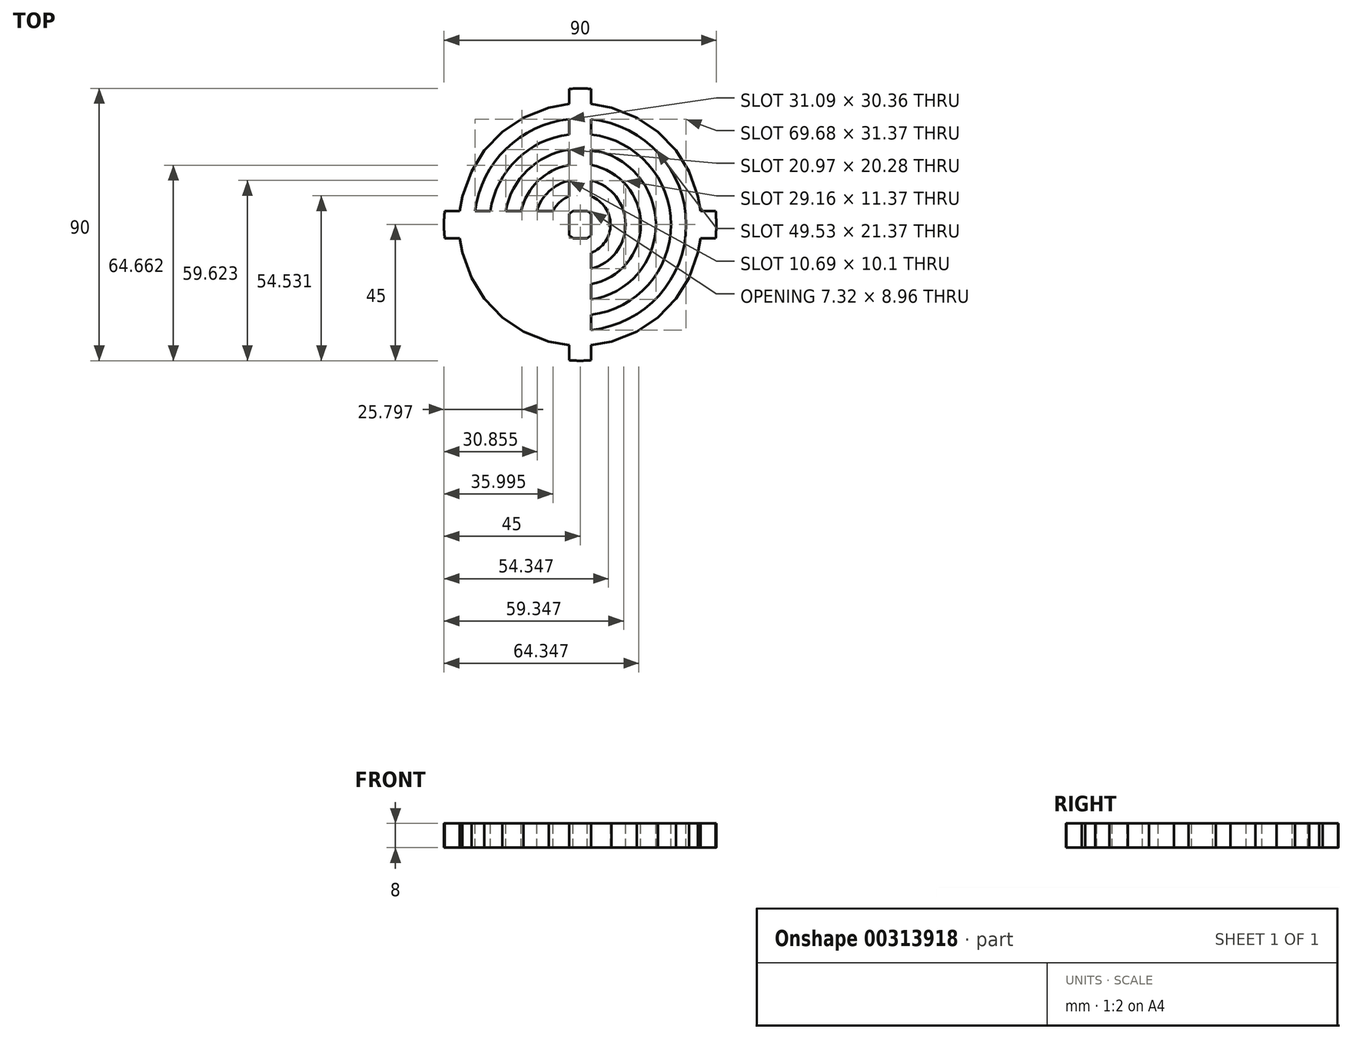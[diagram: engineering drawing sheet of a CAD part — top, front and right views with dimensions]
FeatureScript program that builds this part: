
annotation { "Feature Type Name" : "Feature", "Feature Type Description" : "" }
export const myFeature = defineFeature(function(context is Context, id is Id, definition is map)
    precondition{}
    {
        {
            var Q0;
            Q0=qCreatedBy(makeId("Top.planeOp"),FACE);
            var sketch = newSketch(context, id + "F0", { "sketchPlane" : qUnion([Q0])});
            skCircle(sketch, "E0", {"center": v(0, 0) * mm, "radius": 45 * mm});
            skSolve(sketch);
        }
        {
            var Q0;
            Q0=makeQuery(id+"F0.imprint","IMPRINT",FACE,{"disambiguationData":[TD([[makeQuery(id+"F0.imprint","IMPRINT",EDGE,{"derivedFrom":sQuery(id+"F0.wireOp",EDGE,"E0")}),1.0]])]});
            extrude(context, id + "F1", {"entities" : qUnion([Q0]), "depth" : 8 * mm});
        }
        {
            var Q0;
            Q0=makeQuery(id+"F1.opExtrude","CAP_FACE",FACE,{"disambiguationData":[OSD([sQuery(id+"F0.wireOp",EDGE,"E0")])],"isStart":false});
            var sketch = newSketch(context, id + "F2", { "sketchPlane" : qUnion([Q0])});
            skLineSegment(sketch, "E1", {"start": v(0, 50.25) * mm, "end": v(0, -49.39) * mm, "construction": true});
            skLineSegment(sketch, "E2", {"start": v(-52.78, 0) * mm, "end": v(52.32, 0) * mm, "construction": true});
            skCircle(sketch, "E3", {"center": v(0, 0) * mm, "radius": 40.03 * mm, "construction": true});
            skLineSegment(sketch, "E4", {"start": v(-3.66, 44.85) * mm, "end": v(-3.66, 39.87) * mm});
            skLineSegment(sketch, "E5", {"start": v(-3.66, 39.87) * mm, "end": v(-10.32, 38.68) * mm});
            skLineSegment(sketch, "E6", {"start": v(-10.32, 38.68) * mm, "end": v(-18.69, 35.4) * mm});
            skLineSegment(sketch, "E7", {"start": v(-18.69, 35.4) * mm, "end": v(-25.77, 30.64) * mm});
            skLineSegment(sketch, "E8", {"start": v(-25.77, 30.64) * mm, "end": v(-31.64, 24.53) * mm});
            skLineSegment(sketch, "E9", {"start": v(-31.64, 24.53) * mm, "end": v(-35.95, 17.62) * mm});
            skLineSegment(sketch, "E10", {"start": v(-35.95, 17.62) * mm, "end": v(-38.94, 9.29) * mm});
            skLineSegment(sketch, "E11", {"start": v(-38.94, 9.29) * mm, "end": v(-39.78, 4.48) * mm});
            skLineSegment(sketch, "E12", {"start": v(-39.78, 4.48) * mm, "end": v(-50.5, 4.48) * mm});
            skLineSegment(sketch, "E13", {"start": v(-50.5, 4.48) * mm, "end": v(-45.74, 26.13) * mm});
            skLineSegment(sketch, "E14", {"start": v(-45.74, 26.13) * mm, "end": v(-30.42, 39.87) * mm});
            skLineSegment(sketch, "E15", {"start": v(-30.42, 39.87) * mm, "end": v(-14.4, 46.73) * mm});
            skLineSegment(sketch, "E16", {"start": v(-14.4, 46.73) * mm, "end": v(-3.66, 46.73) * mm});
            skLineSegment(sketch, "E17", {"start": v(-3.66, 46.73) * mm, "end": v(-3.66, 44.85) * mm});
            skLineSegment(sketch, "E18.MirrorCS", {"start": v(3.66, 46.73) * mm, "end": v(3.66, 44.85) * mm});
            skLineSegment(sketch, "E19.MirrorCS", {"start": v(18.69, 35.4) * mm, "end": v(25.77, 30.64) * mm});
            skLineSegment(sketch, "E20.MirrorCS", {"start": v(10.32, 38.68) * mm, "end": v(18.69, 35.4) * mm});
            skLineSegment(sketch, "E21.MirrorCS", {"start": v(25.77, 30.64) * mm, "end": v(31.64, 24.53) * mm});
            skLineSegment(sketch, "E22.MirrorCS", {"start": v(3.66, 39.87) * mm, "end": v(10.32, 38.68) * mm});
            skLineSegment(sketch, "E23.MirrorCS", {"start": v(31.64, 24.53) * mm, "end": v(35.95, 17.62) * mm});
            skLineSegment(sketch, "E24.MirrorCS", {"start": v(3.66, 44.85) * mm, "end": v(3.66, 39.87) * mm});
            skLineSegment(sketch, "E25.MirrorCS", {"start": v(35.95, 17.62) * mm, "end": v(38.94, 9.29) * mm});
            skLineSegment(sketch, "E26.MirrorCS", {"start": v(38.94, 9.29) * mm, "end": v(39.78, 4.48) * mm});
            skLineSegment(sketch, "E27.MirrorCS", {"start": v(52.78, 0) * mm, "end": v(-52.32, 0) * mm, "construction": true});
            skLineSegment(sketch, "E28.MirrorCS", {"start": v(39.78, 4.48) * mm, "end": v(50.5, 4.48) * mm});
            skLineSegment(sketch, "E29.MirrorCS", {"start": v(14.4, 46.73) * mm, "end": v(3.66, 46.73) * mm});
            skLineSegment(sketch, "E30.MirrorCS", {"start": v(45.74, 26.13) * mm, "end": v(30.42, 39.87) * mm});
            skLineSegment(sketch, "E31.MirrorCS", {"start": v(50.5, 4.48) * mm, "end": v(45.74, 26.13) * mm});
            skLineSegment(sketch, "E32.MirrorCS", {"start": v(30.42, 39.87) * mm, "end": v(14.4, 46.73) * mm});
            skLineSegment(sketch, "E33.MirrorCS", {"start": v(3.66, -46.73) * mm, "end": v(3.66, -44.85) * mm});
            skLineSegment(sketch, "E34.MirrorCS", {"start": v(-3.66, -46.73) * mm, "end": v(-3.66, -44.85) * mm});
            skLineSegment(sketch, "E35.MirrorCS", {"start": v(10.32, -38.68) * mm, "end": v(18.69, -35.4) * mm});
            skLineSegment(sketch, "E36.MirrorCS", {"start": v(38.94, -9.29) * mm, "end": v(39.78, -4.48) * mm});
            skLineSegment(sketch, "E37.MirrorCS", {"start": v(18.69, -35.4) * mm, "end": v(25.77, -30.64) * mm});
            skLineSegment(sketch, "E38.MirrorCS", {"start": v(31.64, -24.53) * mm, "end": v(35.95, -17.62) * mm});
            skLineSegment(sketch, "E39.MirrorCS", {"start": v(50.5, -4.48) * mm, "end": v(45.74, -26.13) * mm});
            skLineSegment(sketch, "E40.MirrorCS", {"start": v(-50.5, -4.48) * mm, "end": v(-45.74, -26.13) * mm});
            skLineSegment(sketch, "E41.MirrorCS", {"start": v(35.95, -17.62) * mm, "end": v(38.94, -9.29) * mm});
            skLineSegment(sketch, "E42.MirrorCS", {"start": v(-39.78, -4.48) * mm, "end": v(-50.5, -4.48) * mm});
            skLineSegment(sketch, "E43.MirrorCS", {"start": v(-38.94, -9.29) * mm, "end": v(-39.78, -4.48) * mm});
            skLineSegment(sketch, "E44.MirrorCS", {"start": v(-35.95, -17.62) * mm, "end": v(-38.94, -9.29) * mm});
            skLineSegment(sketch, "E45.MirrorCS", {"start": v(-31.64, -24.53) * mm, "end": v(-35.95, -17.62) * mm});
            skLineSegment(sketch, "E46.MirrorCS", {"start": v(-25.77, -30.64) * mm, "end": v(-31.64, -24.53) * mm});
            skLineSegment(sketch, "E47.MirrorCS", {"start": v(-18.69, -35.4) * mm, "end": v(-25.77, -30.64) * mm});
            skLineSegment(sketch, "E48.MirrorCS", {"start": v(-10.32, -38.68) * mm, "end": v(-18.69, -35.4) * mm});
            skLineSegment(sketch, "E49.MirrorCS", {"start": v(-3.66, -39.87) * mm, "end": v(-10.32, -38.68) * mm});
            skLineSegment(sketch, "E50.MirrorCS", {"start": v(-3.66, -44.85) * mm, "end": v(-3.66, -39.87) * mm});
            skLineSegment(sketch, "E51.MirrorCS", {"start": v(39.78, -4.48) * mm, "end": v(50.5, -4.48) * mm});
            skLineSegment(sketch, "E52.MirrorCS", {"start": v(45.74, -26.13) * mm, "end": v(30.42, -39.87) * mm});
            skLineSegment(sketch, "E53.MirrorCS", {"start": v(3.66, -39.87) * mm, "end": v(10.32, -38.68) * mm});
            skLineSegment(sketch, "E54.MirrorCS", {"start": v(30.42, -39.87) * mm, "end": v(14.4, -46.73) * mm});
            skLineSegment(sketch, "E55.MirrorCS", {"start": v(-45.74, -26.13) * mm, "end": v(-30.42, -39.87) * mm});
            skLineSegment(sketch, "E56.MirrorCS", {"start": v(25.77, -30.64) * mm, "end": v(31.64, -24.53) * mm});
            skLineSegment(sketch, "E57.MirrorCS", {"start": v(-30.42, -39.87) * mm, "end": v(-14.4, -46.73) * mm});
            skLineSegment(sketch, "E58.MirrorCS", {"start": v(14.4, -46.73) * mm, "end": v(3.66, -46.73) * mm});
            skLineSegment(sketch, "E59.MirrorCS", {"start": v(3.66, -44.85) * mm, "end": v(3.66, -39.87) * mm});
            skLineSegment(sketch, "E60.MirrorCS", {"start": v(-14.4, -46.73) * mm, "end": v(-3.66, -46.73) * mm});
            skSolve(sketch);
        }
        {
            var Q0;
            {var subQ0=sQuery(id+"F2.wireOp",EDGE,"E13");Q0=makeQuery(id+"F2.imprint","IMPRINT",FACE,{"disambiguationData":[TD([[makeQuery(id+"F2.imprint","IMPRINT",EDGE,{"derivedFrom":subQ0}),-1.0]])]});}
            var Q1;
            {var subQ0=sQuery(id+"F2.wireOp",EDGE,"E4");Q1=makeQuery(id+"F2.imprint","IMPRINT",FACE,{"disambiguationData":[TD([[makeQuery(id+"F2.imprint","IMPRINT",EDGE,{"derivedFrom":subQ0}),-1.0]])]});}
            var Q2;
            Q2=makeQuery(id+"F2.imprint","IMPRINT",FACE,{"disambiguationData":[TD([[makeQuery(id+"F2.imprint","IMPRINT",EDGE,{"derivedFrom":sQuery(id+"F2.wireOp",EDGE,"E19.MirrorCS")}),1.0]])]});
            var Q3;
            {var subQ0=sQuery(id+"F2.wireOp",EDGE,"E18.MirrorCS");Q3=makeQuery(id+"F2.imprint","IMPRINT",FACE,{"disambiguationData":[TD([[makeQuery(id+"F2.imprint","IMPRINT",EDGE,{"derivedFrom":subQ0}),1.0]])]});}
            var Q4;
            Q4=makeQuery(id+"F2.imprint","IMPRINT",FACE,{"disambiguationData":[TD([[makeQuery(id+"F2.imprint","IMPRINT",EDGE,{"derivedFrom":sQuery(id+"F2.wireOp",EDGE,"E35.MirrorCS")}),-1.0]])]});
            var Q5;
            {var subQ4=sQuery(id+"F2.wireOp",EDGE,"E33.MirrorCS");Q5=makeQuery(id+"F2.imprint","IMPRINT",FACE,{"disambiguationData":[TD([[makeQuery(id+"F2.imprint","IMPRINT",EDGE,{"derivedFrom":subQ4}),-1.0]])]});}
            var Q6;
            {var subQ4=sQuery(id+"F2.wireOp",EDGE,"E43.MirrorCS");Q6=makeQuery(id+"F2.imprint","IMPRINT",FACE,{"disambiguationData":[TD([[makeQuery(id+"F2.imprint","IMPRINT",EDGE,{"derivedFrom":subQ4}),1.0]])]});}
            var Q7;
            {var subQ0=sQuery(id+"F2.wireOp",EDGE,"E34.MirrorCS");Q7=makeQuery(id+"F2.imprint","IMPRINT",FACE,{"disambiguationData":[TD([[makeQuery(id+"F2.imprint","IMPRINT",EDGE,{"derivedFrom":subQ0}),1.0]])]});}
            extrude(context, id + "F3", {"entities" : qUnion([Q0, Q1, Q2, Q3, Q4, Q5, Q6, Q7]), "operationType" : NewBodyOperationType.REMOVE, "oppositeDirection" : true, "depth" : 25 * mm});
        }
        {
            var Q0;
            Q0=makeQuery(id+"F1.opExtrude","CAP_FACE",FACE,{"disambiguationData":[OSD([sQuery(id+"F0.wireOp",EDGE,"E0")])],"isStart":false});
            var sketch = newSketch(context, id + "F4", { "sketchPlane" : qUnion([Q0])});
            skLineSegment(sketch, "E61", {"start": v(0, 48.4) * mm, "end": v(0, -49.9) * mm, "construction": true});
            skPoint(sketch, "E61.endSnap0", {"position": v(0, -45) * mm});
            skPoint(sketch, "E62.endSnap0", {"position": v(-45, 0) * mm});
            skPoint(sketch, "E63.endSnap0", {"position": v(45, 0) * mm});
            skLineSegment(sketch, "E64", {"start": v(-52.35, 0) * mm, "end": v(55.1, 0) * mm, "construction": true});
            skCircle(sketch, "E65", {"center": v(0, 0) * mm, "radius": 35.03 * mm});
            skCircle(sketch, "E66", {"center": v(0, 0) * mm, "radius": 30.03 * mm});
            skCircle(sketch, "E67", {"center": v(0, 0) * mm, "radius": 25.03 * mm});
            skCircle(sketch, "E68", {"center": v(0, 0) * mm, "radius": 20.03 * mm});
            skCircle(sketch, "E69", {"center": v(0, 0) * mm, "radius": 15.03 * mm});
            skCircle(sketch, "E70", {"center": v(0, 0) * mm, "radius": 10.03 * mm});
            skCircle(sketch, "E71", {"center": v(0, 0) * mm, "radius": 5.03 * mm});
            skLineSegment(sketch, "E72.bottom", {"start": v(-3.66, 39.87) * mm, "end": v(3.66, 39.87) * mm});
            skLineSegment(sketch, "E72.top", {"start": v(-3.66, -39.87) * mm, "end": v(3.66, -39.87) * mm});
            skLineSegment(sketch, "E72.left", {"start": v(-3.66, 39.87) * mm, "end": v(-3.66, -39.87) * mm});
            skLineSegment(sketch, "E72.right", {"start": v(3.66, 39.87) * mm, "end": v(3.66, -39.87) * mm});
            skLineSegment(sketch, "E73.bottom", {"start": v(-39.78, -4.48) * mm, "end": v(39.78, -4.48) * mm});
            skLineSegment(sketch, "E73.top", {"start": v(-39.78, 4.48) * mm, "end": v(39.78, 4.48) * mm});
            skLineSegment(sketch, "E73.left", {"start": v(-39.78, -4.48) * mm, "end": v(-39.78, 4.48) * mm});
            skLineSegment(sketch, "E73.right", {"start": v(39.78, -4.48) * mm, "end": v(39.78, 4.48) * mm});
            skSolve(sketch);
        }
        {
            var Q0;
            {var subQ0=sQuery(id+"F4.wireOp",EDGE,"E73.bottom");var subQ1=sQuery(id+"F4.wireOp",EDGE,"E65");var subQ2=makeQuery(id+"F4.imprint","INTERSECT",VERTEX,{"disambiguationData":[OD(0.0)],"derivedFrom":[subQ1,subQ0]});Q0=makeQuery(id+"F4.imprint","IMPRINT",FACE,{"disambiguationData":[TD([[makeQuery(id+"F4.imprint","IMPRINT",EDGE,{"disambiguationData":[TD([[subQ2,-1.0]])],"derivedFrom":subQ1}),1.0]])]});}
            var Q1;
            {var subQ0=sQuery(id+"F4.wireOp",EDGE,"E73.bottom");var subQ1=sQuery(id+"F4.wireOp",EDGE,"E67");var subQ2=makeQuery(id+"F4.imprint","INTERSECT",VERTEX,{"disambiguationData":[OD(0.0)],"derivedFrom":[subQ1,subQ0]});Q1=makeQuery(id+"F4.imprint","IMPRINT",FACE,{"disambiguationData":[TD([[makeQuery(id+"F4.imprint","IMPRINT",EDGE,{"disambiguationData":[TD([[subQ2,-1.0]])],"derivedFrom":subQ1}),1.0]])]});}
            var Q2;
            {var subQ0=sQuery(id+"F4.wireOp",EDGE,"E73.bottom");var subQ1=sQuery(id+"F4.wireOp",EDGE,"E69");var subQ2=makeQuery(id+"F4.imprint","INTERSECT",VERTEX,{"disambiguationData":[OD(0.0)],"derivedFrom":[subQ1,subQ0]});Q2=makeQuery(id+"F4.imprint","IMPRINT",FACE,{"disambiguationData":[TD([[makeQuery(id+"F4.imprint","IMPRINT",EDGE,{"disambiguationData":[TD([[subQ2,-1.0]])],"derivedFrom":subQ1}),1.0]])]});}
            var Q3;
            {var subQ1=sQuery(id+"F4.wireOp",EDGE,"E71");var subQ8=sQuery(id+"F4.wireOp",EDGE,"E73.top");var subQ12=makeQuery(id+"F4.imprint","INTERSECT",VERTEX,{"disambiguationData":[OD(0.0)],"derivedFrom":[subQ1,subQ8]});Q3=makeQuery(id+"F4.imprint","IMPRINT",FACE,{"disambiguationData":[TD([[makeQuery(id+"F4.imprint","IMPRINT",EDGE,{"disambiguationData":[TD([[subQ12,1.0]])],"derivedFrom":subQ1}),1.0]])]});}
            var Q4;
            {var subQ0=sQuery(id+"F4.wireOp",EDGE,"E72.right");var subQ1=sQuery(id+"F4.wireOp",EDGE,"E69");var subQ2=makeQuery(id+"F4.imprint","INTERSECT",VERTEX,{"disambiguationData":[OD(1.0)],"derivedFrom":[subQ1,subQ0]});Q4=makeQuery(id+"F4.imprint","IMPRINT",FACE,{"disambiguationData":[TD([[makeQuery(id+"F4.imprint","IMPRINT",EDGE,{"disambiguationData":[TD([[subQ2,-1.0]])],"derivedFrom":subQ1}),1.0]])]});}
            var Q5;
            {var subQ0=sQuery(id+"F4.wireOp",EDGE,"E72.right");var subQ1=sQuery(id+"F4.wireOp",EDGE,"E67");var subQ2=makeQuery(id+"F4.imprint","INTERSECT",VERTEX,{"disambiguationData":[OD(1.0)],"derivedFrom":[subQ1,subQ0]});Q5=makeQuery(id+"F4.imprint","IMPRINT",FACE,{"disambiguationData":[TD([[makeQuery(id+"F4.imprint","IMPRINT",EDGE,{"disambiguationData":[TD([[subQ2,-1.0]])],"derivedFrom":subQ1}),1.0]])]});}
            var Q6;
            {var subQ0=sQuery(id+"F4.wireOp",EDGE,"E72.right");var subQ1=sQuery(id+"F4.wireOp",EDGE,"E65");var subQ2=makeQuery(id+"F4.imprint","INTERSECT",VERTEX,{"disambiguationData":[OD(1.0)],"derivedFrom":[subQ1,subQ0]});Q6=makeQuery(id+"F4.imprint","IMPRINT",FACE,{"disambiguationData":[TD([[makeQuery(id+"F4.imprint","IMPRINT",EDGE,{"disambiguationData":[TD([[subQ2,-1.0]])],"derivedFrom":subQ1}),1.0]])]});}
            var Q7;
            {var subQ0=sQuery(id+"F4.wireOp",EDGE,"E72.right");var subQ1=sQuery(id+"F4.wireOp",EDGE,"E65");var subQ2=makeQuery(id+"F4.imprint","INTERSECT",VERTEX,{"disambiguationData":[OD(0.0)],"derivedFrom":[subQ1,subQ0]});Q7=makeQuery(id+"F4.imprint","IMPRINT",FACE,{"disambiguationData":[TD([[makeQuery(id+"F4.imprint","IMPRINT",EDGE,{"disambiguationData":[TD([[subQ2,1.0]])],"derivedFrom":subQ1}),1.0]])]});}
            var Q8;
            {var subQ0=sQuery(id+"F4.wireOp",EDGE,"E72.right");var subQ1=sQuery(id+"F4.wireOp",EDGE,"E67");var subQ2=makeQuery(id+"F4.imprint","INTERSECT",VERTEX,{"disambiguationData":[OD(0.0)],"derivedFrom":[subQ1,subQ0]});Q8=makeQuery(id+"F4.imprint","IMPRINT",FACE,{"disambiguationData":[TD([[makeQuery(id+"F4.imprint","IMPRINT",EDGE,{"disambiguationData":[TD([[subQ2,1.0]])],"derivedFrom":subQ1}),1.0]])]});}
            var Q9;
            {var subQ0=sQuery(id+"F4.wireOp",EDGE,"E72.right");var subQ1=sQuery(id+"F4.wireOp",EDGE,"E69");var subQ2=makeQuery(id+"F4.imprint","INTERSECT",VERTEX,{"disambiguationData":[OD(0.0)],"derivedFrom":[subQ1,subQ0]});Q9=makeQuery(id+"F4.imprint","IMPRINT",FACE,{"disambiguationData":[TD([[makeQuery(id+"F4.imprint","IMPRINT",EDGE,{"disambiguationData":[TD([[subQ2,1.0]])],"derivedFrom":subQ1}),1.0]])]});}
            var Q10;
            {var subQ0=sQuery(id+"F4.wireOp",EDGE,"E72.left");var subQ1=sQuery(id+"F4.wireOp",EDGE,"E69");var subQ2=makeQuery(id+"F4.imprint","INTERSECT",VERTEX,{"disambiguationData":[OD(0.0)],"derivedFrom":[subQ1,subQ0]});Q10=makeQuery(id+"F4.imprint","IMPRINT",FACE,{"disambiguationData":[TD([[makeQuery(id+"F4.imprint","IMPRINT",EDGE,{"disambiguationData":[TD([[subQ2,-1.0]])],"derivedFrom":subQ1}),1.0]])]});}
            var Q11;
            {var subQ0=sQuery(id+"F4.wireOp",EDGE,"E72.left");var subQ1=sQuery(id+"F4.wireOp",EDGE,"E67");var subQ2=makeQuery(id+"F4.imprint","INTERSECT",VERTEX,{"disambiguationData":[OD(0.0)],"derivedFrom":[subQ1,subQ0]});Q11=makeQuery(id+"F4.imprint","IMPRINT",FACE,{"disambiguationData":[TD([[makeQuery(id+"F4.imprint","IMPRINT",EDGE,{"disambiguationData":[TD([[subQ2,-1.0]])],"derivedFrom":subQ1}),1.0]])]});}
            var Q12;
            {var subQ0=sQuery(id+"F4.wireOp",EDGE,"E72.left");var subQ1=sQuery(id+"F4.wireOp",EDGE,"E65");var subQ2=makeQuery(id+"F4.imprint","INTERSECT",VERTEX,{"disambiguationData":[OD(0.0)],"derivedFrom":[subQ1,subQ0]});Q12=makeQuery(id+"F4.imprint","IMPRINT",FACE,{"disambiguationData":[TD([[makeQuery(id+"F4.imprint","IMPRINT",EDGE,{"disambiguationData":[TD([[subQ2,-1.0]])],"derivedFrom":subQ1}),1.0]])]});}
            extrude(context, id + "F5", {"entities" : qUnion([Q0, Q1, Q2, Q3, Q4, Q5, Q6, Q7, Q8, Q9, Q10, Q11, Q12]), "operationType" : NewBodyOperationType.REMOVE, "oppositeDirection" : true, "depth" : 25 * mm});
        }
    });
